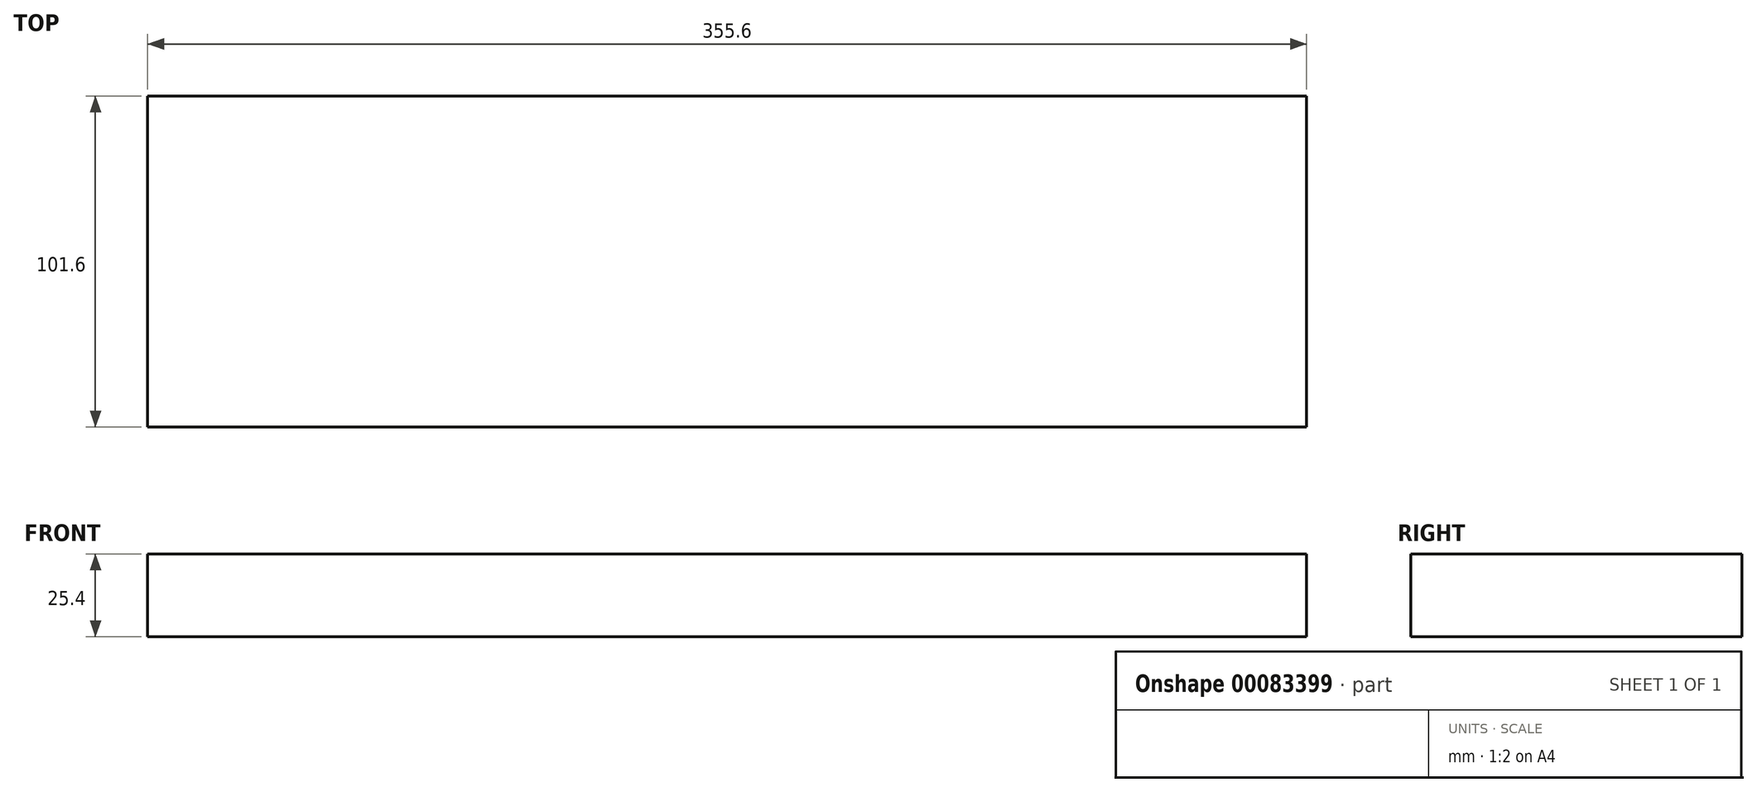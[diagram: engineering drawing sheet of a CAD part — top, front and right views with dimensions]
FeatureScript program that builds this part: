
annotation { "Feature Type Name" : "Feature", "Feature Type Description" : "" }
export const myFeature = defineFeature(function(context is Context, id is Id, definition is map)
    precondition{}
    {
        {
            var Q0;
            Q0=qCreatedBy(makeId("Top.planeOp"),FACE);
            var sketch = newSketch(context, id + "F0", { "sketchPlane" : qUnion([Q0])});
            skLineSegment(sketch, "E0.bottom", {"start": v(-177.8, -50.8) * mm, "end": v(177.8, -50.8) * mm});
            skLineSegment(sketch, "E0.top", {"start": v(-177.8, 50.8) * mm, "end": v(177.8, 50.8) * mm});
            skLineSegment(sketch, "E0.left", {"start": v(-177.8, -50.8) * mm, "end": v(-177.8, 50.8) * mm});
            skLineSegment(sketch, "E0.right", {"start": v(177.8, -50.8) * mm, "end": v(177.8, 50.8) * mm});
            skPoint(sketch, "E0.middle", {"position": v(0, 0) * mm});
            skSolve(sketch);
        }
        {
            var Q0;
            Q0=makeQuery(id+"F0.imprint","IMPRINT",FACE,{"disambiguationData":[TD([[makeQuery(id+"F0.imprint","IMPRINT",EDGE,{"derivedFrom":sQuery(id+"F0.wireOp",EDGE,"E0.bottom")}),1.0]])]});
            extrude(context, id + "F1", {"entities" : qUnion([Q0]), "depth" : 25.4 * mm});
        }
    });
